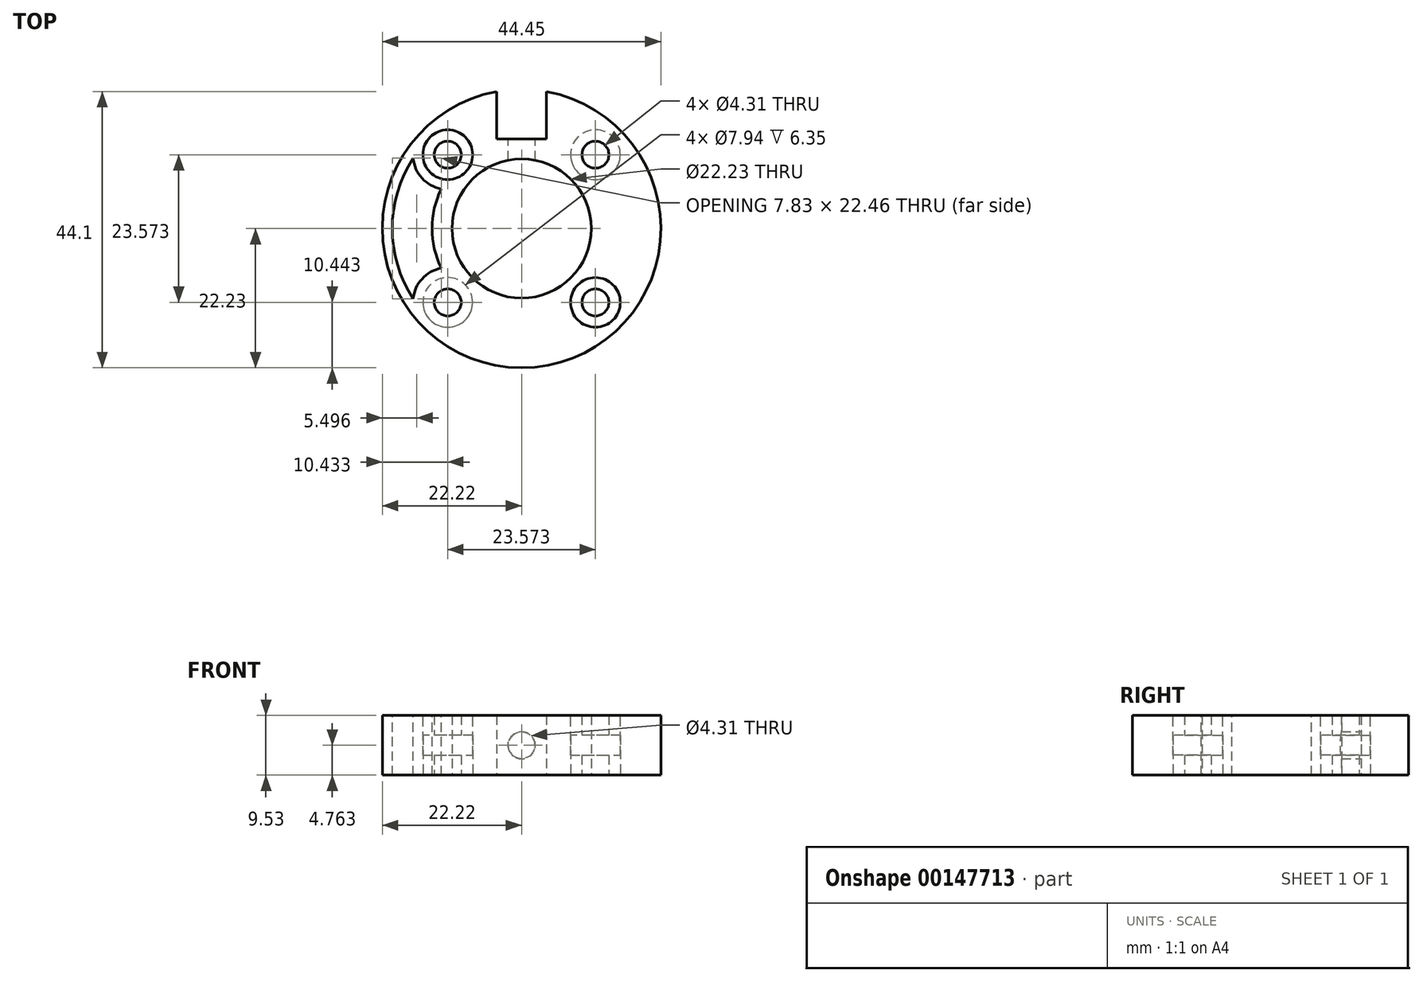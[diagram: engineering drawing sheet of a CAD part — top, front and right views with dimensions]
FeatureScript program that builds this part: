
annotation { "Feature Type Name" : "Feature", "Feature Type Description" : "" }
export const myFeature = defineFeature(function(context is Context, id is Id, definition is map)
    precondition{}
    {
        {
            var Q0;
            Q0=qCreatedBy(makeId("Top.planeOp"),FACE);
            var sketch = newSketch(context, id + "F0", { "sketchPlane" : qUnion([Q0])});
            skCircle(sketch, "E0", {"center": v(0, 0) * mm, "radius": 11.11 * mm});
            skLineSegment(sketch, "E1.bottom", {"start": v(11.79, 11.79) * mm, "end": v(-11.79, 11.79) * mm, "construction": true});
            skLineSegment(sketch, "E1.top", {"start": v(11.79, -11.79) * mm, "end": v(-11.79, -11.79) * mm, "construction": true});
            skLineSegment(sketch, "E1.left", {"start": v(11.79, 11.79) * mm, "end": v(11.79, -11.79) * mm, "construction": true});
            skLineSegment(sketch, "E1.right", {"start": v(-11.79, 11.79) * mm, "end": v(-11.79, -11.79) * mm, "construction": true});
            skCircle(sketch, "E2", {"center": v(-11.79, 11.79) * mm, "radius": 5.56 * mm, "construction": true});
            skLineSegment(sketch, "E3", {"start": v(0, 0) * mm, "end": v(0, 11.11) * mm});
            skLineSegment(sketch, "E4", {"start": v(0, 11.11) * mm, "end": v(0, 14.29) * mm});
            skLineSegment(sketch, "E5.bottom", {"start": v(-3.97, 21.87) * mm, "end": v(3.97, 21.87) * mm, "construction": true});
            skLineSegment(sketch, "E5.top", {"start": v(-3.97, 14.29) * mm, "end": v(3.97, 14.29) * mm});
            skLineSegment(sketch, "E5.left", {"start": v(-3.97, 21.87) * mm, "end": v(-3.97, 14.29) * mm});
            skLineSegment(sketch, "E5.right", {"start": v(3.97, 21.87) * mm, "end": v(3.97, 14.29) * mm});
            skArc(sketch, "E6", {"start": v(-3.97, 21.87) * mm, "mid": v(0, -22.22) * mm, "end": v(3.97, 21.87) * mm});
            skCircle(sketch, "E7", {"center": v(-11.79, 11.79) * mm, "radius": 2.15 * mm});
            skCircle(sketch, "E8", {"center": v(-11.79, -11.79) * mm, "radius": 2.15 * mm});
            skCircle(sketch, "E9", {"center": v(11.79, -11.79) * mm, "radius": 2.15 * mm});
            skCircle(sketch, "E10", {"center": v(11.79, 11.79) * mm, "radius": 2.15 * mm});
            skSolve(sketch);
        }
        {
            var Q0;
            Q0=qSketchRegion(id+"F0",true);
            extrude(context, id + "F1", {"entities" : qUnion([Q0]), "depth" : 9.52 * mm});
        }
        {
            var Q0;
            Q0=makeQuery(id+"F1.opExtrude","SWEPT_FACE",FACE,{"disambiguationData":[OSD([sQuery(id+"F0.wireOp",EDGE,"E5.top")])]});
            var sketch = newSketch(context, id + "F2", { "sketchPlane" : qUnion([Q0])});
            skLineSegment(sketch, "E11", {"start": v(0, 9.53) * mm, "end": v(0, 0) * mm, "construction": true});
            skCircle(sketch, "E12", {"center": v(0, 4.76) * mm, "radius": 2.15 * mm});
            skSolve(sketch);
        }
        {
            var Q0;
            Q0=qSketchRegion(id+"F2",true);
            var Q1;
            Q1=makeQuery(id+"F1.opExtrude","SWEPT_FACE",FACE,{"disambiguationData":[OSD([sQuery(id+"F0.wireOp",EDGE,"E0")])]});
            extrude(context, id + "F3", {"entities" : qUnion([Q0]), "operationType" : NewBodyOperationType.REMOVE, "endBound" : BoundingType.UP_TO_SURFACE, "oppositeDirection" : true, "endBoundEntityFace" : qUnion([Q1]), "depth" : 25.4 * mm});
        }
        {
            var Q0;
            Q0=makeQuery(id+"F1.opExtrude","CAP_FACE",FACE,{"disambiguationData":[OSD([sQuery(id+"F0.wireOp",EDGE,"E0"),sQuery(id+"F0.wireOp",EDGE,"E5.top"),sQuery(id+"F0.wireOp",EDGE,"E5.left"),sQuery(id+"F0.wireOp",EDGE,"E5.right"),sQuery(id+"F0.wireOp",EDGE,"E6"),sQuery(id+"F0.wireOp",EDGE,"E7"),sQuery(id+"F0.wireOp",EDGE,"E8"),sQuery(id+"F0.wireOp",EDGE,"E9"),sQuery(id+"F0.wireOp",EDGE,"E10")])],"isStart":true});
            cPlane(context, id + "F4", {"entities" : qUnion([Q0]), "cplaneType" : CPlaneType.OFFSET, "offset" : 3.17 * mm, "oppositeDirection" : true, "width" : 152.4 * mm, "height" : 152.4 * mm});
        }
        {
            var Q0;
            Q0=makeQuery(id+"F1.opExtrude","CAP_FACE",FACE,{"disambiguationData":[OSD([sQuery(id+"F0.wireOp",EDGE,"E0"),sQuery(id+"F0.wireOp",EDGE,"E5.top"),sQuery(id+"F0.wireOp",EDGE,"E5.left"),sQuery(id+"F0.wireOp",EDGE,"E5.right"),sQuery(id+"F0.wireOp",EDGE,"E6"),sQuery(id+"F0.wireOp",EDGE,"E7"),sQuery(id+"F0.wireOp",EDGE,"E8"),sQuery(id+"F0.wireOp",EDGE,"E9"),sQuery(id+"F0.wireOp",EDGE,"E10")])],"isStart":false});
            cPlane(context, id + "F5", {"entities" : qUnion([Q0]), "cplaneType" : CPlaneType.OFFSET, "offset" : 3.17 * mm, "oppositeDirection" : true, "width" : 152.4 * mm, "height" : 152.4 * mm});
        }
        {
            var Q0;
            Q0=makeQuery(id+"F1.opExtrude","CAP_FACE",FACE,{"disambiguationData":[OSD([sQuery(id+"F0.wireOp",EDGE,"E0"),sQuery(id+"F0.wireOp",EDGE,"E5.top"),sQuery(id+"F0.wireOp",EDGE,"E5.left"),sQuery(id+"F0.wireOp",EDGE,"E5.right"),sQuery(id+"F0.wireOp",EDGE,"E6"),sQuery(id+"F0.wireOp",EDGE,"E7"),sQuery(id+"F0.wireOp",EDGE,"E8"),sQuery(id+"F0.wireOp",EDGE,"E9"),sQuery(id+"F0.wireOp",EDGE,"E10")])],"isStart":false});
            var sketch = newSketch(context, id + "F6", { "sketchPlane" : qUnion([Q0])});
            skCircle(sketch, "E13", {"center": v(-11.79, 11.79) * mm, "radius": 3.97 * mm});
            skCircle(sketch, "E14", {"center": v(11.79, -11.79) * mm, "radius": 3.97 * mm});
            skSolve(sketch);
        }
        {
            var Q0;
            Q0=qSketchRegion(id+"F6",true);
            var Q1;
            Q1=qCreatedBy(id+"F4.planeOp",FACE);
            extrude(context, id + "F7", {"entities" : qUnion([Q0]), "operationType" : NewBodyOperationType.REMOVE, "endBound" : BoundingType.UP_TO_SURFACE, "oppositeDirection" : true, "endBoundEntityFace" : qUnion([Q1]), "depth" : 25.4 * mm});
        }
        {
            var Q0;
            Q0=makeQuery(id+"F1.opExtrude","CAP_FACE",FACE,{"disambiguationData":[OSD([sQuery(id+"F0.wireOp",EDGE,"E0"),sQuery(id+"F0.wireOp",EDGE,"E5.top"),sQuery(id+"F0.wireOp",EDGE,"E5.left"),sQuery(id+"F0.wireOp",EDGE,"E5.right"),sQuery(id+"F0.wireOp",EDGE,"E6"),sQuery(id+"F0.wireOp",EDGE,"E7"),sQuery(id+"F0.wireOp",EDGE,"E8"),sQuery(id+"F0.wireOp",EDGE,"E9"),sQuery(id+"F0.wireOp",EDGE,"E10")])],"isStart":true});
            var sketch = newSketch(context, id + "F8", { "sketchPlane" : qUnion([Q0])});
            skCircle(sketch, "E15", {"center": v(11.79, -11.79) * mm, "radius": 3.97 * mm});
            skCircle(sketch, "E16", {"center": v(-11.79, 11.79) * mm, "radius": 3.97 * mm});
            skSolve(sketch);
        }
        {
            var Q0;
            Q0=qSketchRegion(id+"F8",true);
            var Q1;
            Q1=qCreatedBy(id+"F5.planeOp",FACE);
            extrude(context, id + "F9", {"entities" : qUnion([Q0]), "operationType" : NewBodyOperationType.REMOVE, "endBound" : BoundingType.UP_TO_SURFACE, "oppositeDirection" : true, "endBoundEntityFace" : qUnion([Q1]), "depth" : 25.4 * mm});
        }
        {
            var Q0;
            Q0=makeQuery(id+"F1.opExtrude","CAP_FACE",FACE,{"disambiguationData":[OSD([sQuery(id+"F0.wireOp",EDGE,"E0"),sQuery(id+"F0.wireOp",EDGE,"E5.top"),sQuery(id+"F0.wireOp",EDGE,"E5.left"),sQuery(id+"F0.wireOp",EDGE,"E5.right"),sQuery(id+"F0.wireOp",EDGE,"E6"),sQuery(id+"F0.wireOp",EDGE,"E7"),sQuery(id+"F0.wireOp",EDGE,"E8"),sQuery(id+"F0.wireOp",EDGE,"E9"),sQuery(id+"F0.wireOp",EDGE,"E10")])],"isStart":false});
            var sketch = newSketch(context, id + "F10", { "sketchPlane" : qUnion([Q0])});
            skArc(sketch, "E17", {"start": v(-12.81, 6.33) * mm, "mid": v(-14.29, 0) * mm, "end": v(-12.81, -6.33) * mm});
            skArc(sketch, "E18", {"start": v(-17.31, 11.23) * mm, "mid": v(-15.88, 8.03) * mm, "end": v(-12.81, 6.33) * mm});
            skArc(sketch, "E19", {"start": v(-17.31, 11.23) * mm, "mid": v(-20.64, 0) * mm, "end": v(-17.31, -11.23) * mm});
            skArc(sketch, "E20", {"start": v(-12.81, -6.33) * mm, "mid": v(-15.88, -8.03) * mm, "end": v(-17.31, -11.23) * mm});
            skSolve(sketch);
        }
        {
            var Q0;
            Q0=qSketchRegion(id+"F10",true);
            var Q1;
            Q1=makeQuery(id+"F1.opExtrude","CAP_FACE",FACE,{"disambiguationData":[OSD([sQuery(id+"F0.wireOp",EDGE,"E0"),sQuery(id+"F0.wireOp",EDGE,"E5.top"),sQuery(id+"F0.wireOp",EDGE,"E5.left"),sQuery(id+"F0.wireOp",EDGE,"E5.right"),sQuery(id+"F0.wireOp",EDGE,"E6"),sQuery(id+"F0.wireOp",EDGE,"E7"),sQuery(id+"F0.wireOp",EDGE,"E8"),sQuery(id+"F0.wireOp",EDGE,"E9"),sQuery(id+"F0.wireOp",EDGE,"E10")])],"isStart":true});
            extrude(context, id + "F11", {"entities" : qUnion([Q0]), "operationType" : NewBodyOperationType.REMOVE, "endBound" : BoundingType.UP_TO_SURFACE, "oppositeDirection" : true, "endBoundEntityFace" : qUnion([Q1]), "depth" : 25.4 * mm});
        }
    });
